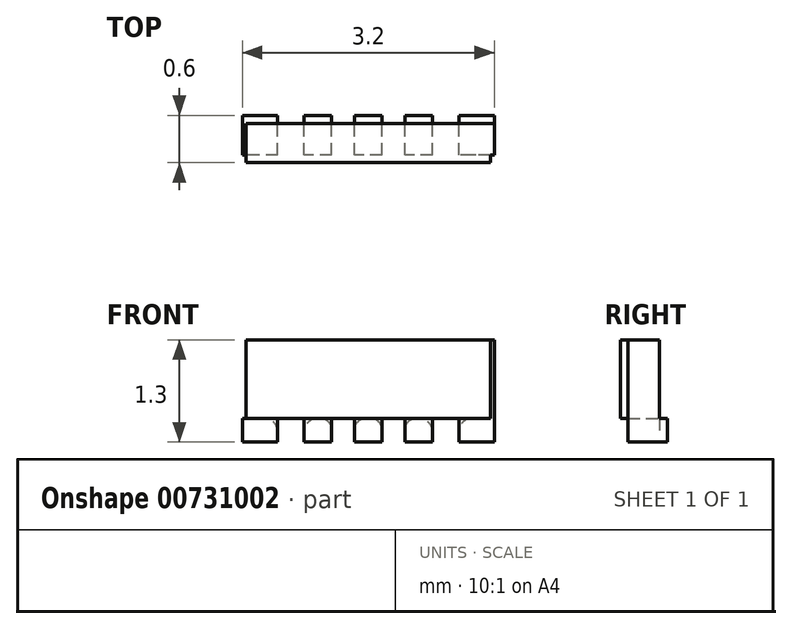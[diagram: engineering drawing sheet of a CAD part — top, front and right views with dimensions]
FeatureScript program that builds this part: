
annotation { "Feature Type Name" : "Feature", "Feature Type Description" : "" }
export const myFeature = defineFeature(function(context is Context, id is Id, definition is map)
    precondition{}
    {
        {
            var Q0;
            Q0=qCreatedBy(makeId("Front.planeOp"),FACE);
            var sketch = newSketch(context, id + "F0", { "sketchPlane" : qUnion([Q0])});
            skLineSegment(sketch, "E0.bottom", {"start": v(1.55, -0.5) * mm, "end": v(-1.55, -0.5) * mm});
            skLineSegment(sketch, "E0.top", {"start": v(1.55, 0.5) * mm, "end": v(-1.55, 0.5) * mm});
            skLineSegment(sketch, "E0.left", {"start": v(1.55, -0.5) * mm, "end": v(1.55, 0.5) * mm});
            skLineSegment(sketch, "E0.right", {"start": v(-1.55, -0.5) * mm, "end": v(-1.55, 0.5) * mm});
            skPoint(sketch, "E0.middle", {"position": v(0, 0) * mm});
            skSolve(sketch);
        }
        {
            var Q0;
            Q0=makeQuery(id+"F0.imprint","IMPRINT",FACE,{"disambiguationData":[TD([[makeQuery(id+"F0.imprint","IMPRINT",EDGE,{"derivedFrom":sQuery(id+"F0.wireOp",EDGE,"E0.bottom")}),-1.0]])]});
            extrude(context, id + "F1", {"entities" : qUnion([Q0]), "depth" : 0.5 * mm, "offsetDistance" : 25 * mm});
        }
        {
            var Q0;
            Q0=makeQuery(id+"F1.opExtrude","SWEPT_FACE",FACE,{"disambiguationData":[OSD([sQuery(id+"F0.wireOp",EDGE,"E0.bottom")])]});
            var sketch = newSketch(context, id + "F2", { "sketchPlane" : qUnion([Q0])});
            skLineSegment(sketch, "E1.top", {"start": v(-1.6, -0.1) * mm, "end": v(-1.15, -0.1) * mm});
            skLineSegment(sketch, "E1.left", {"start": v(-1.6, 0.4) * mm, "end": v(-1.6, -0.1) * mm});
            skLineSegment(sketch, "E1.right", {"start": v(-1.15, 0.4) * mm, "end": v(-1.15, -0.1) * mm});
            skLineSegment(sketch, "E2.top", {"start": v(1.6, -0.1) * mm, "end": v(1.15, -0.1) * mm});
            skLineSegment(sketch, "E2.left", {"start": v(1.6, 0.4) * mm, "end": v(1.6, -0.1) * mm});
            skLineSegment(sketch, "E2.right", {"start": v(1.15, 0.4) * mm, "end": v(1.15, -0.1) * mm});
            skLineSegment(sketch, "E3.bottom", {"start": v(0.81, 0.4) * mm, "end": v(0.46, 0.4) * mm});
            skLineSegment(sketch, "E3.top", {"start": v(0.81, -0.1) * mm, "end": v(0.46, -0.1) * mm});
            skLineSegment(sketch, "E3.left", {"start": v(0.81, 0.4) * mm, "end": v(0.81, -0.1) * mm});
            skLineSegment(sketch, "E3.right", {"start": v(0.46, 0.4) * mm, "end": v(0.46, -0.1) * mm});
            skLineSegment(sketch, "E4.bottom", {"start": v(0.17, 0.4) * mm, "end": v(-0.18, 0.4) * mm});
            skLineSegment(sketch, "E4.top", {"start": v(0.17, -0.1) * mm, "end": v(-0.18, -0.1) * mm});
            skLineSegment(sketch, "E4.left", {"start": v(0.17, 0.4) * mm, "end": v(0.17, -0.1) * mm});
            skLineSegment(sketch, "E4.right", {"start": v(-0.18, 0.4) * mm, "end": v(-0.18, -0.1) * mm});
            skLineSegment(sketch, "E5.bottom", {"start": v(-0.47, 0.4) * mm, "end": v(-0.82, 0.4) * mm});
            skLineSegment(sketch, "E5.top", {"start": v(-0.47, -0.1) * mm, "end": v(-0.82, -0.1) * mm});
            skLineSegment(sketch, "E5.left", {"start": v(-0.47, 0.4) * mm, "end": v(-0.47, -0.1) * mm});
            skLineSegment(sketch, "E5.right", {"start": v(-0.82, 0.4) * mm, "end": v(-0.82, -0.1) * mm});
            skLineSegment(sketch, "E6", {"start": v(-1.15, 0.4) * mm, "end": v(-1.6, 0.4) * mm});
            skLineSegment(sketch, "E7", {"start": v(1.6, 0.4) * mm, "end": v(1.15, 0.4) * mm});
            skSolve(sketch);
        }
        {
            var Q0;
            Q0 = qSketchRegion(id + "F2", true);
            extrude(context, id + "F3", {"entities" : qUnion([Q0]), "operationType" : NewBodyOperationType.ADD, "depth" : 0.3 * mm, "offsetDistance" : 25 * mm});
        }
        {
            var Q0;
            Q0=makeQuery(id+"F1.opExtrude","SWEPT_FACE",FACE,{"disambiguationData":[OSD([sQuery(id+"F0.wireOp",EDGE,"E0.left")])]});
            var sketch = newSketch(context, id + "F4", { "sketchPlane" : qUnion([Q0])});
            skLineSegment(sketch, "E8.bottom", {"start": v(-0.4, 0.5) * mm, "end": v(0, 0.5) * mm});
            skLineSegment(sketch, "E8.top", {"start": v(-0.4, -0.5) * mm, "end": v(0, -0.5) * mm});
            skLineSegment(sketch, "E8.left", {"start": v(-0.4, 0.5) * mm, "end": v(-0.4, -0.5) * mm});
            skLineSegment(sketch, "E8.right", {"start": v(0, 0.5) * mm, "end": v(0, -0.5) * mm});
            skSolve(sketch);
        }
        {
            var Q0;
            Q0 = qSketchRegion(id + "F4", true);
            extrude(context, id + "F5", {"entities" : qUnion([Q0]), "operationType" : NewBodyOperationType.ADD, "depth" : 0.05 * mm, "offsetDistance" : 25 * mm});
        }
        {
            var Q0;
            {var subQ0=sQuery(id+"F2.wireOp",EDGE,"E3.right");Q0=makeQuery(id+"FYcJlgKefGR5XeR_1.1.F3.boolean.opBoolean","SPLIT",EDGE,{"disambiguationData":[topologyDisambiguationEdgeConnected([makeQuery(id+"F1.opExtrude","SWEPT_FACE",FACE,{"disambiguationData":[OSD([sQuery(id+"F0.wireOp",EDGE,"E0.top")])]})])],"derivedFrom":makeQuery(id+"FYcJlgKefGR5XeR_1.1.F3.opExtrude","CAP_EDGE",EDGE,{"disambiguationData":[OSD([subQ0])],"isStart":true})});}
            var Q1;
            {var subQ0=sQuery(id+"F2.wireOp",EDGE,"E4.left");Q1=makeQuery(id+"FYcJlgKefGR5XeR_1.1.F3.boolean.opBoolean","SPLIT",EDGE,{"disambiguationData":[topologyDisambiguationEdgeConnected([makeQuery(id+"F1.opExtrude","SWEPT_FACE",FACE,{"disambiguationData":[OSD([sQuery(id+"F0.wireOp",EDGE,"E0.top")])]})])],"derivedFrom":makeQuery(id+"FYcJlgKefGR5XeR_1.1.F3.opExtrude","CAP_EDGE",EDGE,{"disambiguationData":[OSD([subQ0])],"isStart":true})});}
            var Q2;
            {var subQ0=sQuery(id+"F2.wireOp",EDGE,"E4.right");Q2=makeQuery(id+"FYcJlgKefGR5XeR_1.1.F3.boolean.opBoolean","SPLIT",EDGE,{"disambiguationData":[topologyDisambiguationEdgeConnected([makeQuery(id+"F1.opExtrude","SWEPT_FACE",FACE,{"disambiguationData":[OSD([sQuery(id+"F0.wireOp",EDGE,"E0.top")])]})])],"derivedFrom":makeQuery(id+"FYcJlgKefGR5XeR_1.1.F3.opExtrude","CAP_EDGE",EDGE,{"disambiguationData":[OSD([subQ0])],"isStart":true})});}
            var Q3;
            {var subQ0=sQuery(id+"F2.wireOp",EDGE,"E5.left");Q3=makeQuery(id+"FYcJlgKefGR5XeR_1.1.F3.boolean.opBoolean","SPLIT",EDGE,{"disambiguationData":[topologyDisambiguationEdgeConnected([makeQuery(id+"F1.opExtrude","SWEPT_FACE",FACE,{"disambiguationData":[OSD([sQuery(id+"F0.wireOp",EDGE,"E0.top")])]})])],"derivedFrom":makeQuery(id+"FYcJlgKefGR5XeR_1.1.F3.opExtrude","CAP_EDGE",EDGE,{"disambiguationData":[OSD([subQ0])],"isStart":true})});}
            var Q4;
            {var subQ0=sQuery(id+"F2.wireOp",EDGE,"E5.left");Q4=makeQuery(id+"F3.boolean.opBoolean","SPLIT",EDGE,{"disambiguationData":[topologyDisambiguationEdgeConnected([makeQuery(id+"F1.opExtrude","SWEPT_FACE",FACE,{"disambiguationData":[OSD([sQuery(id+"F0.wireOp",EDGE,"E0.bottom")])]})])],"derivedFrom":makeQuery(id+"F3.opExtrude","CAP_EDGE",EDGE,{"disambiguationData":[OSD([subQ0])],"isStart":true})});}
            var Q5;
            {var subQ0=sQuery(id+"F2.wireOp",EDGE,"E4.right");Q5=makeQuery(id+"F3.boolean.opBoolean","SPLIT",EDGE,{"disambiguationData":[topologyDisambiguationEdgeConnected([makeQuery(id+"F1.opExtrude","SWEPT_FACE",FACE,{"disambiguationData":[OSD([sQuery(id+"F0.wireOp",EDGE,"E0.bottom")])]})])],"derivedFrom":makeQuery(id+"F3.opExtrude","CAP_EDGE",EDGE,{"disambiguationData":[OSD([subQ0])],"isStart":true})});}
            var Q6;
            {var subQ0=sQuery(id+"F2.wireOp",EDGE,"E4.left");Q6=makeQuery(id+"F3.boolean.opBoolean","SPLIT",EDGE,{"disambiguationData":[topologyDisambiguationEdgeConnected([makeQuery(id+"F1.opExtrude","SWEPT_FACE",FACE,{"disambiguationData":[OSD([sQuery(id+"F0.wireOp",EDGE,"E0.bottom")])]})])],"derivedFrom":makeQuery(id+"F3.opExtrude","CAP_EDGE",EDGE,{"disambiguationData":[OSD([subQ0])],"isStart":true})});}
            var Q7;
            {var subQ0=sQuery(id+"F2.wireOp",EDGE,"E3.right");Q7=makeQuery(id+"F3.boolean.opBoolean","SPLIT",EDGE,{"disambiguationData":[topologyDisambiguationEdgeConnected([makeQuery(id+"F1.opExtrude","SWEPT_FACE",FACE,{"disambiguationData":[OSD([sQuery(id+"F0.wireOp",EDGE,"E0.bottom")])]})])],"derivedFrom":makeQuery(id+"F3.opExtrude","CAP_EDGE",EDGE,{"disambiguationData":[OSD([subQ0])],"isStart":true})});}
            fillet(context, id + "F6", {"entities" : qUnion([Q0, Q1, Q2, Q3, Q4, Q5, Q6, Q7]), "radius" : 0.14 * mm, "tangentPropagation" : true, "allowEdgeOverflow" : false});
        }
        {
            var Q0;
            {var subQ0=sQuery(id+"F2.wireOp",EDGE,"E2.right");Q0=makeQuery(id+"FYcJlgKefGR5XeR_1.1.F3.boolean.opBoolean","SPLIT",EDGE,{"disambiguationData":[topologyDisambiguationEdgeConnected([makeQuery(id+"F1.opExtrude","SWEPT_FACE",FACE,{"disambiguationData":[OSD([sQuery(id+"F0.wireOp",EDGE,"E0.top")])]})])],"derivedFrom":makeQuery(id+"FYcJlgKefGR5XeR_1.1.F3.opExtrude","CAP_EDGE",EDGE,{"disambiguationData":[OSD([subQ0])],"isStart":true})});}
            var Q1;
            {var subQ0=sQuery(id+"F2.wireOp",EDGE,"E3.left");Q1=makeQuery(id+"FYcJlgKefGR5XeR_1.1.F3.boolean.opBoolean","SPLIT",EDGE,{"disambiguationData":[topologyDisambiguationEdgeConnected([makeQuery(id+"F1.opExtrude","SWEPT_FACE",FACE,{"disambiguationData":[OSD([sQuery(id+"F0.wireOp",EDGE,"E0.top")])]})])],"derivedFrom":makeQuery(id+"FYcJlgKefGR5XeR_1.1.F3.opExtrude","CAP_EDGE",EDGE,{"disambiguationData":[OSD([subQ0])],"isStart":true})});}
            var Q2;
            {var subQ0=sQuery(id+"F2.wireOp",EDGE,"E5.right");Q2=makeQuery(id+"FYcJlgKefGR5XeR_1.1.F3.boolean.opBoolean","SPLIT",EDGE,{"disambiguationData":[topologyDisambiguationEdgeConnected([makeQuery(id+"F1.opExtrude","SWEPT_FACE",FACE,{"disambiguationData":[OSD([sQuery(id+"F0.wireOp",EDGE,"E0.top")])]})])],"derivedFrom":makeQuery(id+"FYcJlgKefGR5XeR_1.1.F3.opExtrude","CAP_EDGE",EDGE,{"disambiguationData":[OSD([subQ0])],"isStart":true})});}
            var Q3;
            {var subQ0=sQuery(id+"F2.wireOp",EDGE,"E1.right");Q3=makeQuery(id+"FYcJlgKefGR5XeR_1.1.F3.boolean.opBoolean","SPLIT",EDGE,{"disambiguationData":[topologyDisambiguationEdgeConnected([makeQuery(id+"F1.opExtrude","SWEPT_FACE",FACE,{"disambiguationData":[OSD([sQuery(id+"F0.wireOp",EDGE,"E0.top")])]})])],"derivedFrom":makeQuery(id+"FYcJlgKefGR5XeR_1.1.F3.opExtrude","CAP_EDGE",EDGE,{"disambiguationData":[OSD([subQ0])],"isStart":true})});}
            var Q4;
            {var subQ0=sQuery(id+"F2.wireOp",EDGE,"E5.right");Q4=makeQuery(id+"F3.boolean.opBoolean","SPLIT",EDGE,{"disambiguationData":[topologyDisambiguationEdgeConnected([makeQuery(id+"F1.opExtrude","SWEPT_FACE",FACE,{"disambiguationData":[OSD([sQuery(id+"F0.wireOp",EDGE,"E0.bottom")])]})])],"derivedFrom":makeQuery(id+"F3.opExtrude","CAP_EDGE",EDGE,{"disambiguationData":[OSD([subQ0])],"isStart":true})});}
            var Q5;
            {var subQ0=sQuery(id+"F2.wireOp",EDGE,"E1.right");Q5=makeQuery(id+"F3.boolean.opBoolean","SPLIT",EDGE,{"disambiguationData":[topologyDisambiguationEdgeConnected([makeQuery(id+"F1.opExtrude","SWEPT_FACE",FACE,{"disambiguationData":[OSD([sQuery(id+"F0.wireOp",EDGE,"E0.bottom")])]})])],"derivedFrom":makeQuery(id+"F3.opExtrude","CAP_EDGE",EDGE,{"disambiguationData":[OSD([subQ0])],"isStart":true})});}
            var Q6;
            {var subQ0=sQuery(id+"F2.wireOp",EDGE,"E3.left");Q6=makeQuery(id+"F3.boolean.opBoolean","SPLIT",EDGE,{"disambiguationData":[topologyDisambiguationEdgeConnected([makeQuery(id+"F1.opExtrude","SWEPT_FACE",FACE,{"disambiguationData":[OSD([sQuery(id+"F0.wireOp",EDGE,"E0.bottom")])]})])],"derivedFrom":makeQuery(id+"F3.opExtrude","CAP_EDGE",EDGE,{"disambiguationData":[OSD([subQ0])],"isStart":true})});}
            var Q7;
            {var subQ0=sQuery(id+"F2.wireOp",EDGE,"E2.right");Q7=makeQuery(id+"F3.boolean.opBoolean","SPLIT",EDGE,{"disambiguationData":[topologyDisambiguationEdgeConnected([makeQuery(id+"F1.opExtrude","SWEPT_FACE",FACE,{"disambiguationData":[OSD([sQuery(id+"F0.wireOp",EDGE,"E0.bottom")])]})])],"derivedFrom":makeQuery(id+"F3.opExtrude","CAP_EDGE",EDGE,{"disambiguationData":[OSD([subQ0])],"isStart":true})});}
            fillet(context, id + "F7", {"entities" : qUnion([Q0, Q1, Q2, Q3, Q4, Q5, Q6, Q7]), "radius" : 0.17 * mm, "tangentPropagation" : true, "allowEdgeOverflow" : false});
        }
    });
